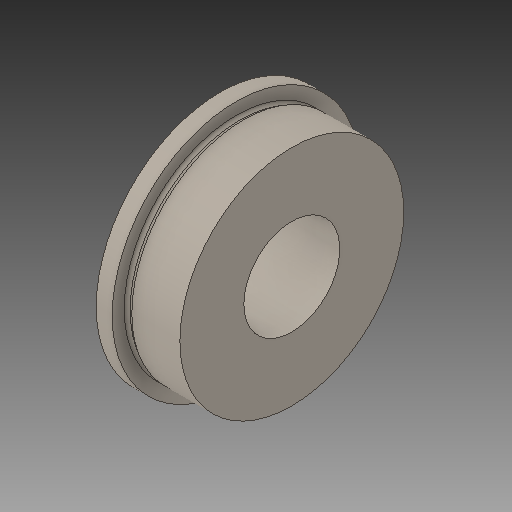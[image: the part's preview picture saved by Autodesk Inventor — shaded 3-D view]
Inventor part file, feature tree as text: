
AUTODESK INVENTOR PART (.ipt)
format: ipt  version: 2017 (Build 210142000, 142)  size: 146,432 bytes
history: native  units: in
note: dims shown in document units (in); Inventor stores cm internally (conversion verified against a paired STEP export)
features: revolve x1
ambient origin geometry x8: Origin, YZ Plane, XZ Plane, XY Plane, X Axis, Y Axis, Z Axis, Center Point
bodies: Solid1 (feature_tree)
feature tree (1):
  revolve  "Revolve1"  [1 undecoded]
note: 1 required parameter value undecoded (feature->parameter linkage not recoverable at this tier; creation-order binding heuristic only, values carry confidence <= 0.55)
